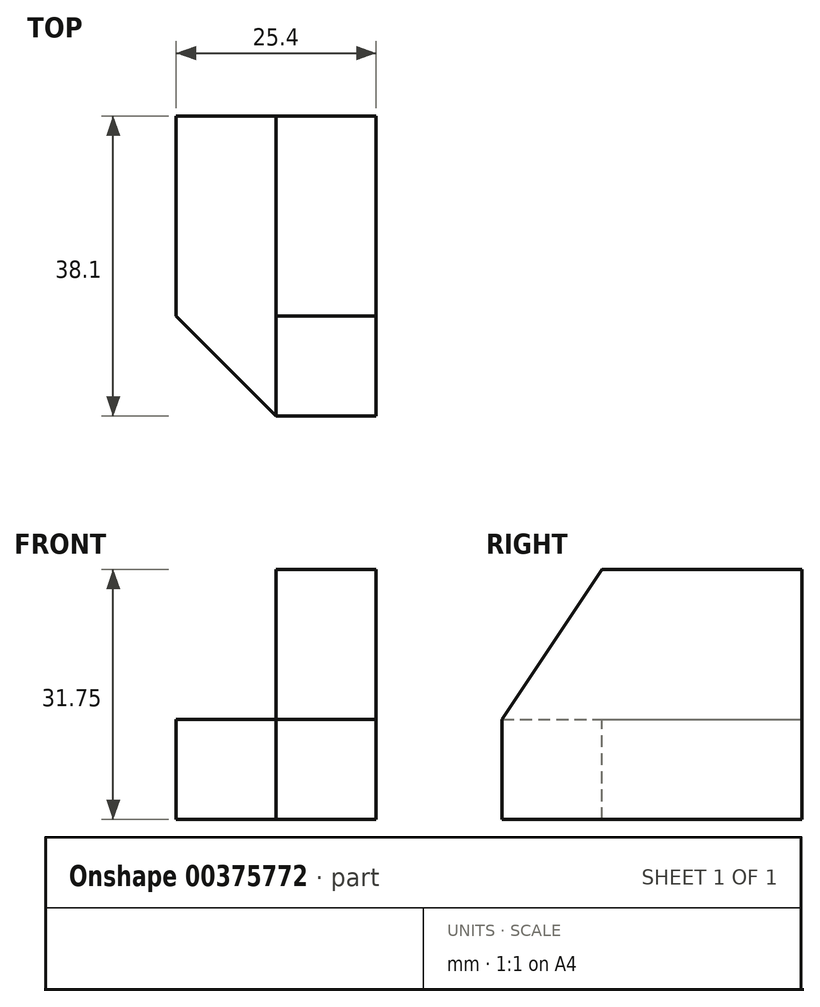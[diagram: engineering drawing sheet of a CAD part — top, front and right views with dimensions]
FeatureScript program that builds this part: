
annotation { "Feature Type Name" : "Feature", "Feature Type Description" : "" }
export const myFeature = defineFeature(function(context is Context, id is Id, definition is map)
    precondition{}
    {
        {
            var Q0;
            Q0=qCreatedBy(makeId("Front.planeOp"),FACE);
            var sketch = newSketch(context, id + "F0", { "sketchPlane" : qUnion([Q0])});
            skLineSegment(sketch, "E0", {"start": v(0, 0) * mm, "end": v(25.4, 0) * mm});
            skLineSegment(sketch, "E1", {"start": v(25.4, 0) * mm, "end": v(25.4, 31.75) * mm});
            skLineSegment(sketch, "E2", {"start": v(25.4, 31.75) * mm, "end": v(12.7, 31.75) * mm});
            skLineSegment(sketch, "E3", {"start": v(12.7, 31.75) * mm, "end": v(12.7, 12.7) * mm});
            skLineSegment(sketch, "E4", {"start": v(12.7, 12.7) * mm, "end": v(0, 12.7) * mm});
            skLineSegment(sketch, "E5", {"start": v(0, 12.7) * mm, "end": v(0, 0) * mm});
            skSolve(sketch);
        }
        {
            var Q0;
            Q0 = qSketchRegion(id + "F0", true);
            extrude(context, id + "F1", {"entities" : qUnion([Q0]), "depth" : 38.1 * mm});
        }
        {
            var Q0;
            Q0=makeQuery(id+"F1.opExtrude","SWEPT_FACE",FACE,{"disambiguationData":[OSD([sQuery(id+"F0.wireOp",EDGE,"E3")])]});
            var sketch = newSketch(context, id + "F2", { "sketchPlane" : qUnion([Q0])});
            skLineSegment(sketch, "E6", {"start": v(25.4, 31.75) * mm, "end": v(38.1, 12.7) * mm});
            skSolve(sketch);
        }
        {
            var Q0;
            {var subQ0=sQuery(id+"F2.wireOp",EDGE,"E6");Q0=makeQuery(id+"F2.imprint","IMPRINT",FACE,{"disambiguationData":[TD([[makeQuery(id+"F2.imprint","IMPRINT",EDGE,{"derivedFrom":subQ0}),1.0]])]});}
            extrude(context, id + "F3", {"entities" : qUnion([Q0]), "operationType" : NewBodyOperationType.REMOVE, "oppositeDirection" : true, "depth" : 25.4 * mm});
        }
        {
            var Q0;
            Q0=makeQuery(id+"F1.opExtrude","SWEPT_FACE",FACE,{"disambiguationData":[OSD([sQuery(id+"F0.wireOp",EDGE,"E4")])]});
            var sketch = newSketch(context, id + "F4", { "sketchPlane" : qUnion([Q0])});
            skLineSegment(sketch, "E7", {"start": v(12.7, -38.1) * mm, "end": v(0, -25.4) * mm});
            skSolve(sketch);
        }
        {
            var Q0;
            {var subQ0=sQuery(id+"F4.wireOp",EDGE,"E7");Q0=makeQuery(id+"F4.imprint","IMPRINT",FACE,{"disambiguationData":[TD([[makeQuery(id+"F4.imprint","IMPRINT",EDGE,{"derivedFrom":subQ0}),1.0]])]});}
            extrude(context, id + "F5", {"entities" : qUnion([Q0]), "operationType" : NewBodyOperationType.REMOVE, "oppositeDirection" : true, "depth" : 25.4 * mm});
        }
    });
